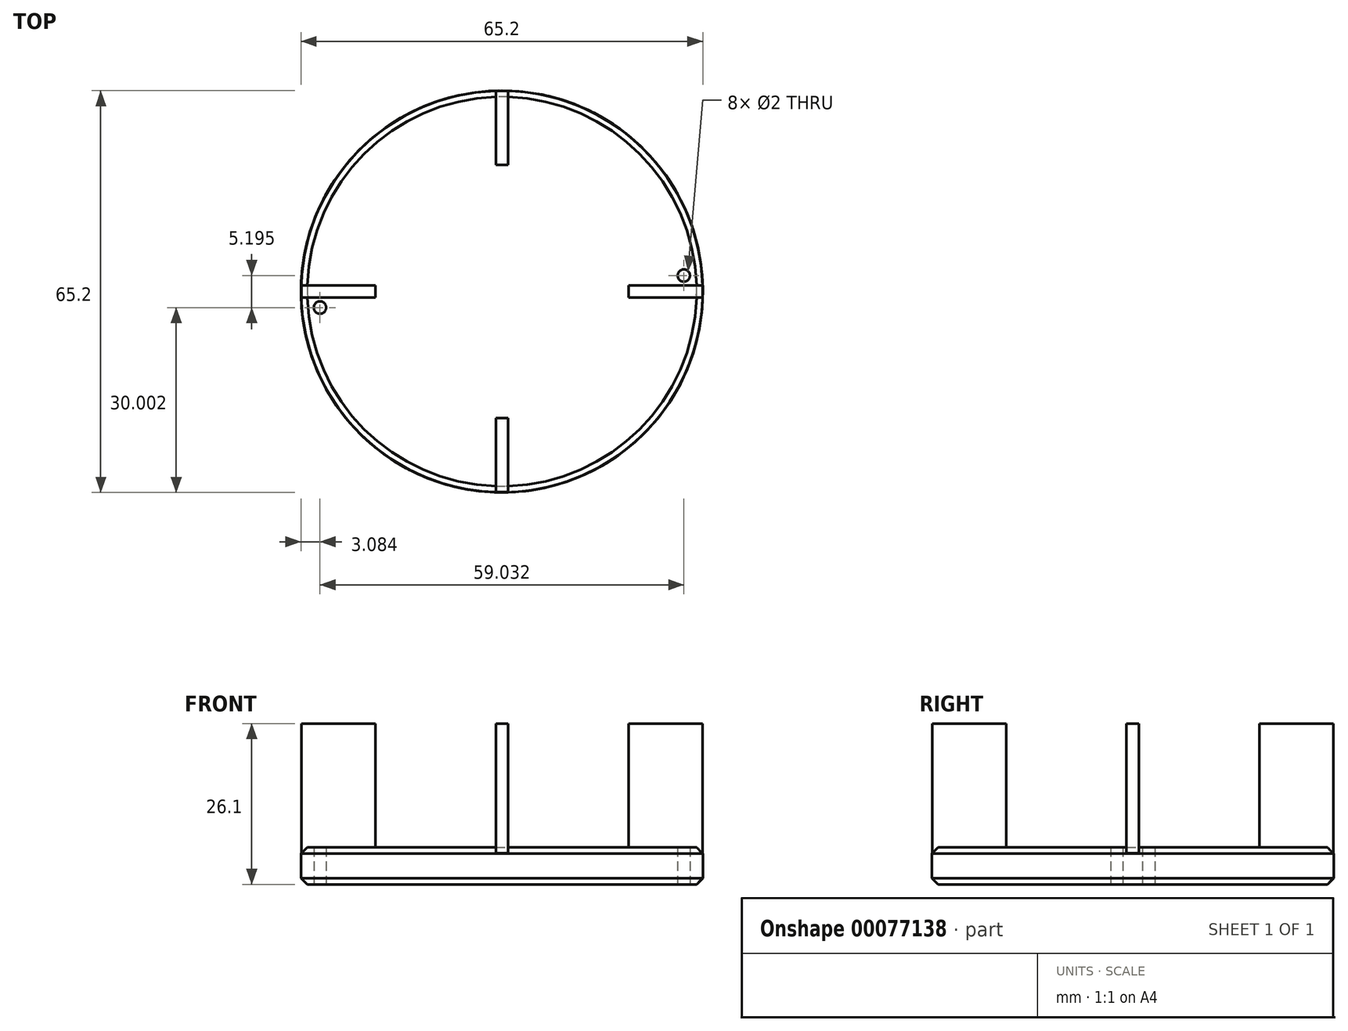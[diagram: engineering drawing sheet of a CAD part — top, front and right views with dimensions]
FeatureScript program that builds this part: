
annotation { "Feature Type Name" : "Feature", "Feature Type Description" : "" }
export const myFeature = defineFeature(function(context is Context, id is Id, definition is map)
    precondition{}
    {
        {
            var Q0;
            Q0=qCreatedBy(makeId("Top.planeOp"),FACE);
            var sketch = newSketch(context, id + "F0", { "sketchPlane" : qUnion([Q0])});
            skCircle(sketch, "E0", {"center": v(0, 0) * mm, "radius": 32.6 * mm});
            skLineSegment(sketch, "E1", {"start": v(-47.7, 126.94) * mm, "end": v(47.43, -126.73) * mm});
            skSolve(sketch);
        }
        {
            var Q0;
            Q0=makeQuery(id+"F0.imprint","IMPRINT",FACE,{"disambiguationData":[TD([[makeQuery(id+"F0.imprint","IMPRINT",EDGE,{"derivedFrom":sQuery(id+"F0.wireOp",EDGE,"E0")}),1.0]])]});
            extrude(context, id + "F1", {"entities" : qUnion([Q0]), "depth" : 6 * mm});
        }
        {
            var Q0;
            Q0=makeQuery(id+"F1.opExtrude","CAP_EDGE",EDGE,{"disambiguationData":[OSD([sQuery(id+"F0.wireOp",EDGE,"E0")])],"isStart":false});
            var Q1;
            Q1=makeQuery(id+"F1.opExtrude","CAP_EDGE",EDGE,{"disambiguationData":[OSD([sQuery(id+"F0.wireOp",EDGE,"E0")])],"isStart":true});
            chamfer(context, id + "F2", {"entities" : qUnion([Q0, Q1]), "width" : 1 * mm, "tangentPropagation" : true});
        }
        {
            var Q0;
            Q0=qCreatedBy(makeId("Front.planeOp"),FACE);
            var sketch = newSketch(context, id + "F3", { "sketchPlane" : qUnion([Q0])});
            skLineSegment(sketch, "E2.bottom", {"start": v(-32.54, 3.1) * mm, "end": v(-20.54, 3.1) * mm});
            skLineSegment(sketch, "E2.top", {"start": v(-32.54, 26.1) * mm, "end": v(-20.54, 26.1) * mm});
            skLineSegment(sketch, "E2.left", {"start": v(-32.54, 3.1) * mm, "end": v(-32.54, 26.1) * mm});
            skLineSegment(sketch, "E2.right", {"start": v(-20.54, 3.1) * mm, "end": v(-20.54, 26.1) * mm});
            skLineSegment(sketch, "E3", {"start": v(0, 87.8) * mm, "end": v(0, -75.87) * mm});
            skSolve(sketch);
        }
        {
            var Q0;
            Q0=makeQuery(id+"F3.imprint","IMPRINT",FACE,{"disambiguationData":[TD([[makeQuery(id+"F3.imprint","IMPRINT",EDGE,{"derivedFrom":sQuery(id+"F3.wireOp",EDGE,"E2.bottom")}),1.0]])]});
            extrude(context, id + "F4", {"entities" : qUnion([Q0]), "operationType" : NewBodyOperationType.ADD, "depth" : 2 * mm, "symmetric" : true});
        }
        {
            var Q0;
            Q0=makeQuery(id+"F1.opExtrude","SWEPT_BODY",BODY,{"disambiguationData":[OSD([sQuery(id+"F0.wireOp",EDGE,"E0")])]});
            var Q1;
            {var subQ0=sQuery(id+"F0.wireOp",EDGE,"E0");Q1=makeQuery(id+"F2.opChamfer","BLEND_FACE",FACE,{"disambiguationData":[OSD([subQ0]),TDD([makeQuery(id+"F1.opExtrude","CAP_EDGE",EDGE,{"disambiguationData":[OSD([subQ0])],"isStart":false})])]});}
            circularPattern(context, id + "F5", {"entities" : qUnion([Q0]), "axis" : qUnion([Q1]), "angle" : 360 * degree, "instanceCount" : 4, "oppositeDirection" : true, "equalSpace" : true, "computeTransformsWithoutBuiltin" : true});
        }
        {
            var Q0;
            Q0=qCreatedBy(makeId("Top.planeOp"),FACE);
            var sketch = newSketch(context, id + "F6", { "sketchPlane" : qUnion([Q0])});
            skCircle(sketch, "E4", {"center": v(-29.52, -2.6) * mm, "radius": 1 * mm});
            skLineSegment(sketch, "E5", {"start": v(-46.31, 0) * mm, "end": v(35.5, 0) * mm, "construction": true});
            skLineSegment(sketch, "E6", {"start": v(-25.75, 25.75) * mm, "end": v(0, 0) * mm, "construction": true});
            skLineSegment(sketch, "E7", {"start": v(0, 0) * mm, "end": v(27.68, -27.68) * mm, "construction": true});
            skCircle(sketch, "E8.1.0", {"center": v(29.52, 2.6) * mm, "radius": 1 * mm});
            skPoint(sketch, "E8.center", {"position": v(0, 0) * mm});
            skLineSegment(sketch, "E8.anchor1", {"start": v(0, 0) * mm, "end": v(-29.52, -2.6) * mm, "construction": true});
            skLineSegment(sketch, "E8.anchor2", {"start": v(0, 0) * mm, "end": v(29.52, 2.6) * mm, "construction": true});
            skSolve(sketch);
        }
        {
            var Q0;
            Q0=makeQuery(id+"F6.imprint","IMPRINT",FACE,{"disambiguationData":[TD([[makeQuery(id+"F6.imprint","IMPRINT",EDGE,{"derivedFrom":sQuery(id+"F6.wireOp",EDGE,"E4")}),1.0]])]});
            var Q1;
            Q1=makeQuery(id+"F6.imprint","IMPRINT",FACE,{"disambiguationData":[TD([[makeQuery(id+"F6.imprint","IMPRINT",EDGE,{"derivedFrom":sQuery(id+"F6.wireOp",EDGE,"E8.1.0")}),1.0]])]});
            extrude(context, id + "F7", {"entities" : qUnion([Q0, Q1]), "operationType" : NewBodyOperationType.REMOVE, "depth" : 25 * mm});
        }
    });
